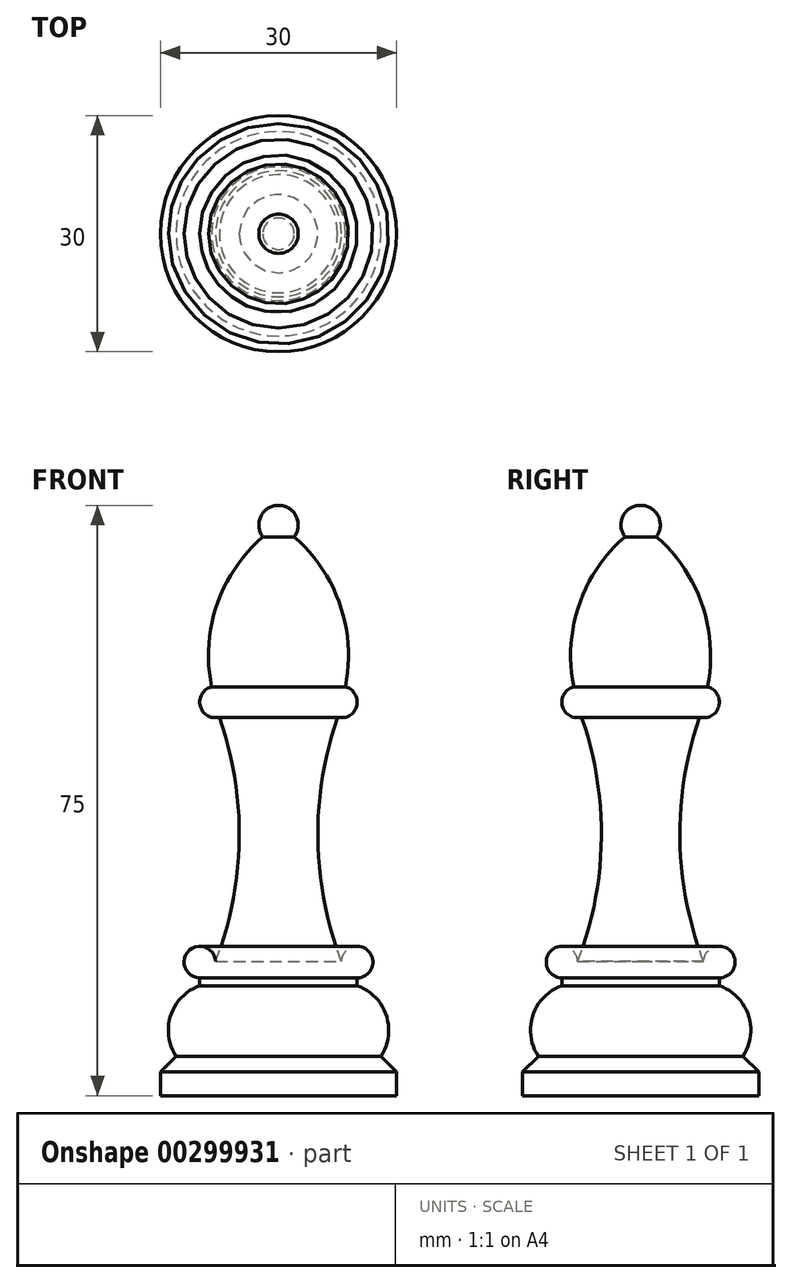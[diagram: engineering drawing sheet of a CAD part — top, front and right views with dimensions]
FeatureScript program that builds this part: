
annotation { "Feature Type Name" : "Feature", "Feature Type Description" : "" }
export const myFeature = defineFeature(function(context is Context, id is Id, definition is map)
    precondition{}
    {
        {
            var Q0;
            Q0=qCreatedBy(makeId("Front.planeOp"),FACE);
            var sketch = newSketch(context, id + "F0", { "sketchPlane" : qUnion([Q0])});
            skArc(sketch, "E0", {"start": v(2, -4) * mm, "mid": v(2.24, -1.38) * mm, "end": v(0, 0) * mm});
            skArc(sketch, "E1", {"start": v(8.5, -23.06) * mm, "mid": v(7.82, -12.65) * mm, "end": v(2, -4) * mm});
            skLineSegment(sketch, "E2", {"start": v(7.5, -26.93) * mm, "end": v(8.5, -26.93) * mm});
            skArc(sketch, "E3", {"start": v(7.5, -26.93) * mm, "mid": v(5, -42.49) * mm, "end": v(8, -57.95) * mm});
            skArc(sketch, "E4", {"start": v(10, -60.03) * mm, "mid": v(11.44, -56.64) * mm, "end": v(8, -57.95) * mm});
            skLineSegment(sketch, "E5", {"start": v(10, -60.03) * mm, "end": v(10, -61.03) * mm});
            skArc(sketch, "E6", {"start": v(13, -70) * mm, "mid": v(13.69, -64.78) * mm, "end": v(10, -61.03) * mm});
            skLineSegment(sketch, "E7", {"start": v(13, -70) * mm, "end": v(15, -72) * mm});
            skLineSegment(sketch, "E8", {"start": v(15, -72) * mm, "end": v(15, -75) * mm});
            skLineSegment(sketch, "E9", {"start": v(15, -75) * mm, "end": v(0, -75) * mm});
            skLineSegment(sketch, "E10", {"start": v(0, -75) * mm, "end": v(0, 0) * mm});
            skArc(sketch, "E11", {"start": v(8.5, -26.93) * mm, "mid": v(10, -25) * mm, "end": v(8.5, -23.06) * mm});
            skSolve(sketch);
        }
        {
            var Q0;
            Q0=makeQuery(id+"F0.imprint","IMPRINT",FACE,{"disambiguationData":[TD([[makeQuery(id+"F0.imprint","IMPRINT",EDGE,{"derivedFrom":sQuery(id+"F0.wireOp",EDGE,"E0")}),1.0]])]});
            var Q1;
            Q1=sQuery(id+"F0.wireOp",EDGE,"E10");
            revolve(context, id + "F1", {"entities" : qUnion([Q0]), "axis" : qUnion([Q1]), "revolveType" : RevolveType.FULL});
        }
    });
